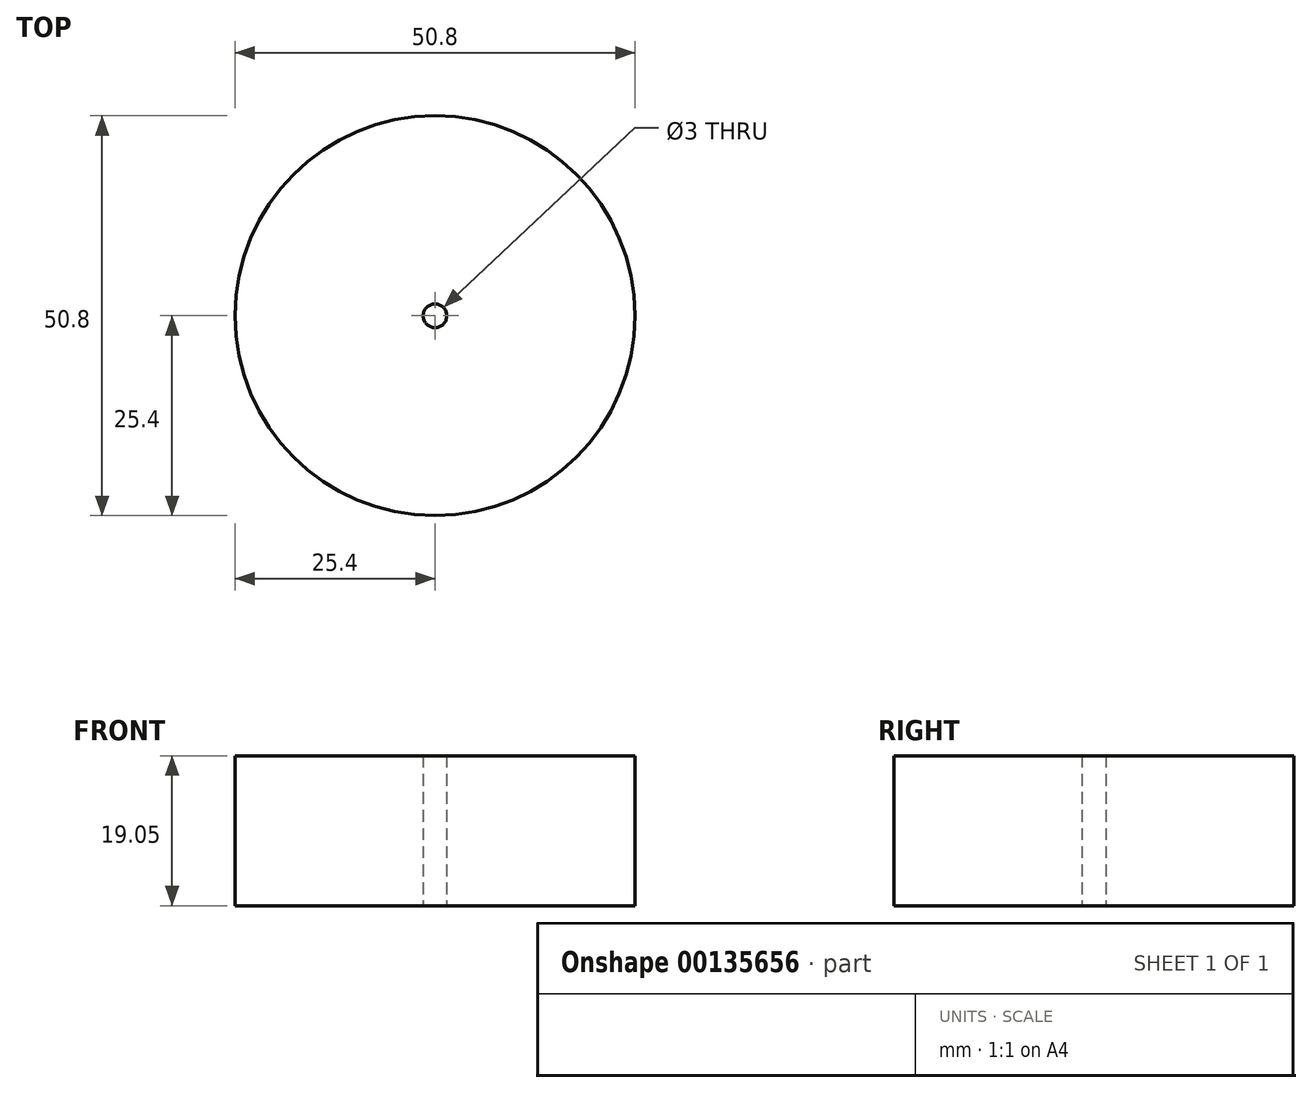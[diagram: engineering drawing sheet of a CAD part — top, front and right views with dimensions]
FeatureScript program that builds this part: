
annotation { "Feature Type Name" : "Feature", "Feature Type Description" : "" }
export const myFeature = defineFeature(function(context is Context, id is Id, definition is map)
    precondition{}
    {
        {
            var Q0;
            Q0=qCreatedBy(makeId("Top.planeOp"),FACE);
            var sketch = newSketch(context, id + "F0", { "sketchPlane" : qUnion([Q0])});
            skCircle(sketch, "E0", {"center": v(0, 0) * mm, "radius": 1.5 * mm});
            skCircle(sketch, "E1", {"center": v(0, 0) * mm, "radius": 25.4 * mm});
            skSolve(sketch);
        }
        {
            var Q0;
            Q0=makeQuery(id+"F0.imprint","IMPRINT",FACE,{"disambiguationData":[TD([[makeQuery(id+"F0.imprint","IMPRINT",EDGE,{"derivedFrom":sQuery(id+"F0.wireOp",EDGE,"E0")}),-1.0]])]});
            extrude(context, id + "F1", {"entities" : qUnion([Q0]), "depth" : 19.05 * mm});
        }
    });
